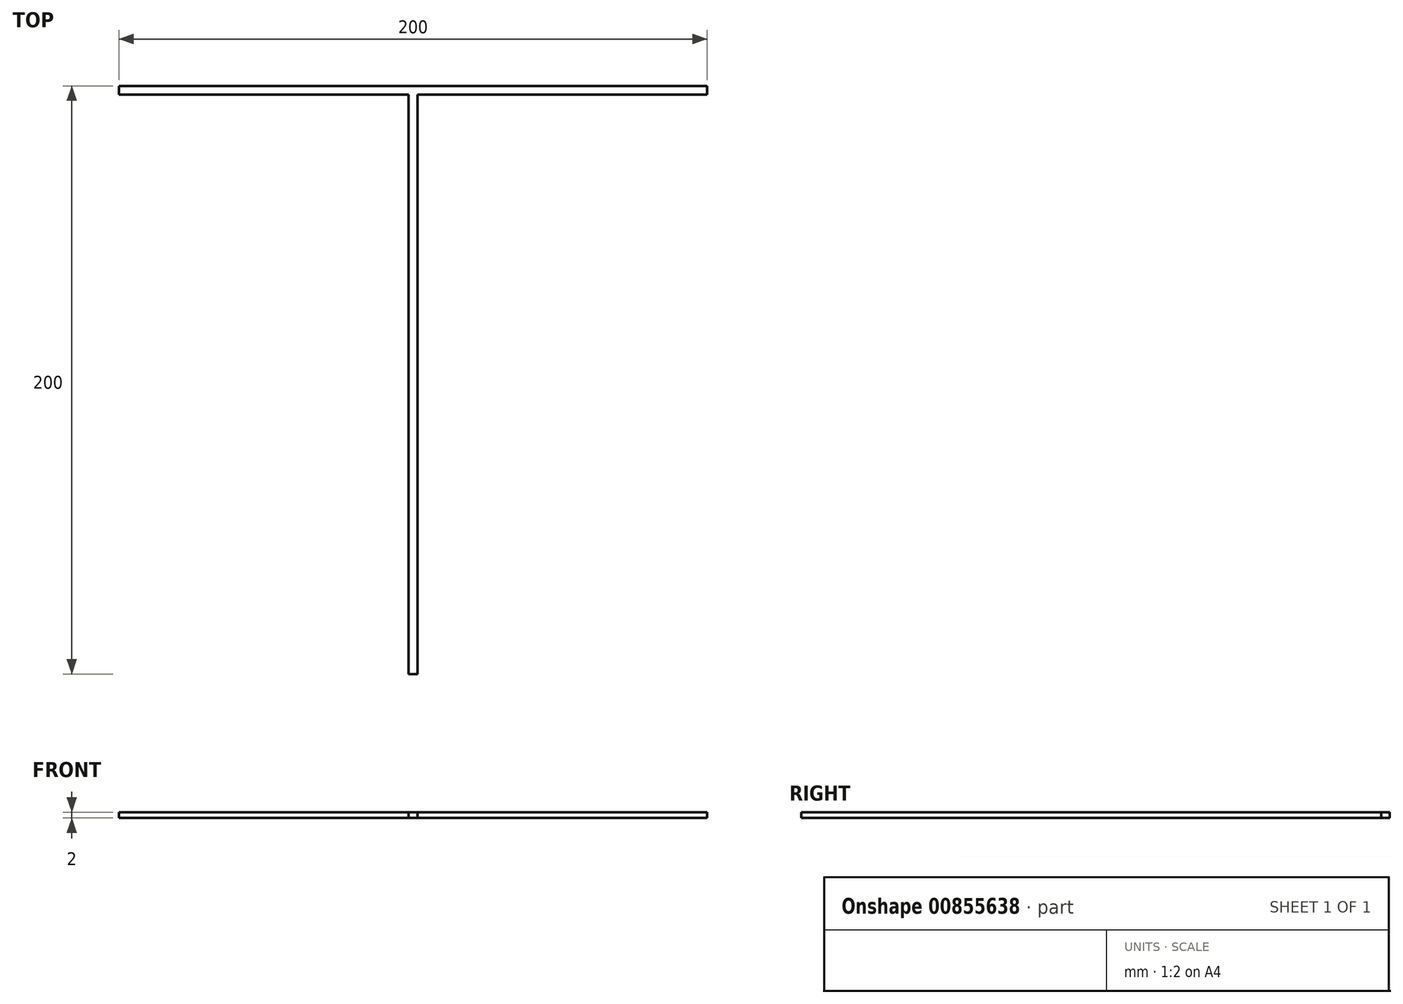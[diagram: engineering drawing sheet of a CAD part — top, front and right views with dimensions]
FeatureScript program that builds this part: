
annotation { "Feature Type Name" : "Feature", "Feature Type Description" : "" }
export const myFeature = defineFeature(function(context is Context, id is Id, definition is map)
    precondition{}
    {
        {
            var Q0;
            Q0=qCreatedBy(makeId("Top.planeOp"),FACE);
            var sketch = newSketch(context, id + "F0", { "sketchPlane" : qUnion([Q0])});
            skLineSegment(sketch, "E0.bottom", {"start": v(0, 0) * mm, "end": v(3, 0) * mm});
            skLineSegment(sketch, "E0.top", {"start": v(0, -200) * mm, "end": v(3, -200) * mm});
            skLineSegment(sketch, "E0.left", {"start": v(0, 0) * mm, "end": v(0, -200) * mm});
            skLineSegment(sketch, "E0.right", {"start": v(3, 0) * mm, "end": v(3, -200) * mm});
            skLineSegment(sketch, "E1.bottom", {"start": v(0, 0) * mm, "end": v(-98.5, 0) * mm});
            skLineSegment(sketch, "E1.top", {"start": v(0, -3) * mm, "end": v(-98.5, -3) * mm});
            skLineSegment(sketch, "E1.left", {"start": v(0, 0) * mm, "end": v(0, -3) * mm});
            skLineSegment(sketch, "E1.right", {"start": v(-98.5, 0) * mm, "end": v(-98.5, -3) * mm});
            skLineSegment(sketch, "E2.bottom", {"start": v(3, 0) * mm, "end": v(101.5, 0) * mm});
            skLineSegment(sketch, "E2.top", {"start": v(3, -3) * mm, "end": v(101.5, -3) * mm});
            skLineSegment(sketch, "E2.left", {"start": v(3, 0) * mm, "end": v(3, -3) * mm});
            skLineSegment(sketch, "E2.right", {"start": v(101.5, 0) * mm, "end": v(101.5, -3) * mm});
            skSolve(sketch);
        }
        {
            var Q0;
            Q0=makeQuery(id+"F0.imprint","IMPRINT",FACE,{"disambiguationData":[TD([[makeQuery(id+"F0.imprint","IMPRINT",EDGE,{"derivedFrom":sQuery(id+"F0.wireOp",EDGE,"E1.bottom")}),1.0]])]});
            var Q1;
            Q1=makeQuery(id+"F0.imprint","IMPRINT",FACE,{"disambiguationData":[TD([[makeQuery(id+"F0.imprint","IMPRINT",EDGE,{"derivedFrom":sQuery(id+"F0.wireOp",EDGE,"E0.bottom")}),-1.0]])]});
            var Q2;
            Q2=makeQuery(id+"F0.imprint","IMPRINT",FACE,{"disambiguationData":[TD([[makeQuery(id+"F0.imprint","IMPRINT",EDGE,{"derivedFrom":sQuery(id+"F0.wireOp",EDGE,"E2.bottom")}),-1.0]])]});
            extrude(context, id + "F1", {"entities" : qUnion([Q0, Q1, Q2]), "depth" : 2 * mm, "offsetDistance" : 25 * mm});
        }
    });
